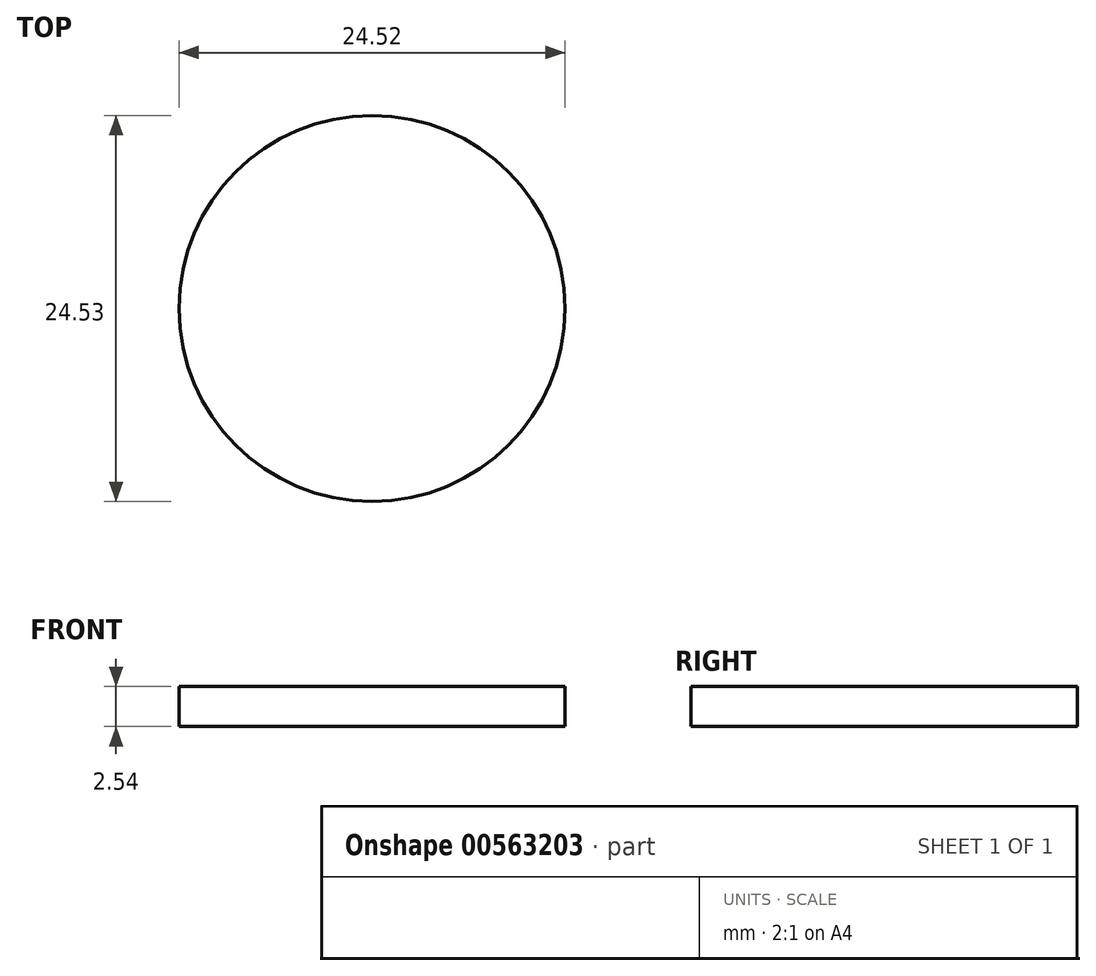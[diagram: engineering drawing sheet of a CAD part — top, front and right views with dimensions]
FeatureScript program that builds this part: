
annotation { "Feature Type Name" : "Feature", "Feature Type Description" : "" }
export const myFeature = defineFeature(function(context is Context, id is Id, definition is map)
    precondition{}
    {
        {
            var Q0;
            Q0=qCreatedBy(makeId("Top.planeOp"),FACE);
            var sketch = newSketch(context, id + "F0", { "sketchPlane" : qUnion([Q0])});
            skCircle(sketch, "E0", {"center": v(-53.77, -9.07) * mm, "radius": 25.4 * mm});
            skCircle(sketch, "E1", {"center": v(-35.02, -44.56) * mm, "radius": 12.26 * mm});
            skSolve(sketch);
        }
        {
            var Q0;
            Q0=makeQuery(id+"F0.imprint","IMPRINT",FACE,{"disambiguationData":[TD([[makeQuery(id+"F0.imprint","IMPRINT",EDGE,{"derivedFrom":sQuery(id+"F0.wireOp",EDGE,"E1")}),1.0]])]});
            extrude(context, id + "F1", {"entities" : qUnion([Q0]), "oppositeDirection" : true, "depth" : 2.54 * mm, "offsetDistance" : 25.4 * mm});
        }
    });
